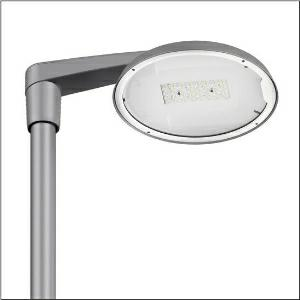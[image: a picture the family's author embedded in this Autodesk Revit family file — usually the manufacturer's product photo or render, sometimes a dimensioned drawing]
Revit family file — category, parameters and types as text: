
# Revit family: dl_50_iq_mini___st0_5a_5xa248b41f08ge_5cd5
name_source: partatom
category: Lighting Fixtures
units: mm (PartAtom-declared; Revit-internal decimal feet)

## family parameters
Cut with Voids When Loaded = No
Host = Face
Light Source = No
Part Type = Normal
Room Calculation Point = No
Round Connector Dimension = Use Diameter
Shared = No

## types (1)
- --- (1 x LED, 5190 lm, 31.2 W, 4000K)
    Apparent Load = 31 VA
    CIE Flux Codes = 41 75 97 100 100
    Color Rendering = 70
    Color Temperature = 4000K
    Default Elevation = 1800 mm
    Description = DL 50 iQ mini, mast luminaire, primary light control with lens, of PMMA, primary optical cover: cover, of toughened safety glass, transparent, light distribution: ST0.5a, light emission: direct distribution, primary light characteristic: asymmetric, installation type: side-entry, post-top, LED, High Power LED, rated luminous flux: 5.190lm, luminous efficacy: 166lm/W, light colour: 740, colour temperature: 4000K, control gear: iQ Street-Remote, control: optimised constant luminous flux control (CLO 2.0), Desk-Remote (wireless, voltage-free reading and setting of iQ features in the workshop via application-optimized NFC function/RFID function), Light-Fading, Smart-Wire, Night-Set, Lumen-Switch, Temp-Guard, Auto-Match, Street-Remote, mains connection: 230..240V, AC, 50/60Hz, connection cable pre-assembled, cable length: 6,5m, start of lifetime: 31W, end of service life: 32W, reduction: 15W, luminaire housing, of diecast aluminium, powder-coated, SITECO metallic grey (DB 702S), inclination adjustable: 0°, 5°, 10° (post-top) | 0°, -5°, -10°, -15° (side-entry), please order mast post-top element or mast side-entry element separately, diameter: 500mm, height: 115mm, post-top: for spigot size d x l = 76 x 100mm; with reducer (optional accessory) 60 x 100mm | side-entry: for spigot size d x l = 60 x 100mm; with reducer (optional accessory) 42 x 100mm, mounting height: 4..6m, protection rating (complete): IP66, insulation class (complete): insulation class II (safety insulation), certification: CE, ENEC, ENEC+, VDE, impact resistance: IK08, permissible operating ambient temperature for outdoor applications: -25..+40°C, standard-compliant lighting for roads and squares, packaging unit: 1 piece

Light Distribution: ST0.5a
    Height = 115 mm
    Lamp = 1 x LED
    Lamp Light Flux = 5190 lm
    Lamp Power = 31.2 W
    Lamp count = 1
    Length = 500 mm
    Luminous efficacy = 166 lm/W
    Manufacturer = Siteco
    ModVariant = No
    Model = 5XA248B41F08GE
    Number of Poles = 1
    OnlyDefault = Yes
    Power Factor = 1
    Product Name = DL 50 iQ mini | ST0.5a
    Product group = mast luminaire | pylon top
    ProductGroupID = 6100
    Protection Class = Protection class II
    Protection Degree = IP 66
    RLX_Detail_Level = 1
    RLX_Emergency_Light_Flux = 0 lm
    RLX_Emergency_Type = 0
    RLX_Emergency_Type_DB = No
    RlxData = <blob elided: 126765 chars, md5=a9fa8086>
    Socket = socket
    Standby Power = 0 W
    System Light Flux = 5190 lm
    System Power = 31 W
    Type Comments = factory setting: luminous flux: 100 % | dim-lin: 254 | 325 mA
    Type Image = l_1251794.jpg
    URL = http://relux.com
    VarID = @adj_142757
    Voltage = 0 V
    Weight = 0.00 kg
    Width = 0 mm  [stored 0 ft]

note: [stored X ft] marks values corroborated as IEEE doubles in the binary element streams (Revit-internal decimal feet)

## geometry (parser evidence)
native form markers: Blend x4, Sweep x10
no freeform markers — native parametric forms only
